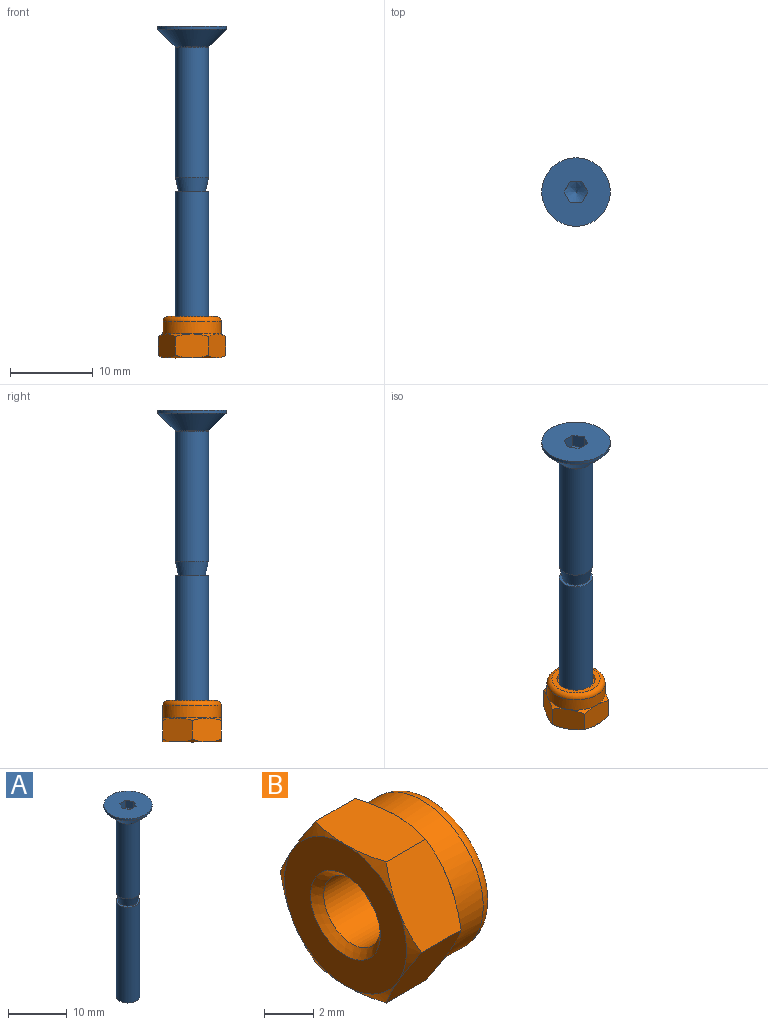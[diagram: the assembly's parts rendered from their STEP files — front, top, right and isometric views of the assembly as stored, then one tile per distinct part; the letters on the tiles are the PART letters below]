
ASSEMBLY  parts=2 mates=1
PART A: 16 faces, bbox 8.4x8.4x40.1 mm
  f0: plane 4x4mm, normal (0,0,-1), area 12.6mm2, adj f1
  f1: revolved ~20x4mm, area 251.3mm2, adj f0,f2
  f2: plane 4x4mm, normal (0,0,1), area 4.3mm2, adj f1,f3
  f3: revolved ~4x4mm, area 20.4mm2, adj f2,f4
  f4: revolved ~15.66x4mm, area 196.7mm2, adj f3,f5
  f5: revolved ~4.09x4.09mm, area 1.6mm2, adj f4,f6
  f6: revolved ~8.25x8.25mm, area 56.9mm2, adj f5,f7
  f7: revolved ~8.25x8.25mm, area 21mm2, adj f6,f8
  f8: plane 8.25x8.25mm, normal (0,0,1), area 48mm2, adj f7,f9,f10,f11,f12,f13,f14
  f9: plane 1.61x1.25mm, normal (-0.87,0.5,0), area 2.3mm2, adj f8,f10,f14,f15
  f10: plane 1.73x1.56mm, normal (0,1,0), area 2.3mm2, adj f8,f9,f11,f15
  f11: plane 1.61x1.25mm, normal (0.87,0.5,0), area 2.3mm2, adj f8,f10,f12,f15
  f12: plane 1.61x1.25mm, normal (0.87,-0.5,0), area 2.3mm2, adj f8,f11,f13,f15
  f13: plane 1.73x1.56mm, normal (0,-1,0), area 2.3mm2, adj f8,f12,f14,f15
  f14: plane 1.61x1.25mm, normal (-0.87,-0.5,0), area 2.3mm2, adj f8,f9,f13,f15
  f15: revolved ~2.89x2.89mm, area 6.4mm2, adj f9,f10,f11,f12,f13,f14
PART B: 30 faces, bbox 5x8.1x8.1 mm
  f0: cone r=1.81mm half-angle=45deg, axis (-1,0,0), area 6.1mm2, adj f1,f29
  f1: cylinder r=1.62mm len=3.24mm, axis (1,0,0), area 21.8mm2, adj f0,f2
  f2: cone r=1.81mm half-angle=45deg, axis (1,0,0), area 6.1mm2, adj f1,f3
  f3: cylinder r=2mm len=4mm, axis (1,0,0), area 6.6mm2, adj f2,f28
  f4: cylinder r=1.62mm len=3.24mm, axis (1,0,0), area 10.7mm2, adj f27,f28
  f5: cylinder r=2.3mm len=4.6mm, axis (1,0,0), area 7.6mm2, adj f26,f27
  f6: torus R=2.9mm, axis (1,0,0), area 19.4mm2, adj f9,f26
  f7: cone r=4.38mm half-angle=60deg, axis (-1,0,0), area 0.8mm2, adj f9,f13,f15
  f8: cone r=4.38mm half-angle=60deg, axis (-1,0,0), area 0.8mm2, adj f9,f12,f17
  f9: cylinder r=3.5mm len=7mm, axis (1,0,0), area 33mm2, adj f6,f7,f8,f22,f23,f24,f25
  f10: cone r=4.38mm half-angle=60deg, axis (1,0,0), area 0.8mm2, adj f13,f15,f29
  f11: cone r=4.38mm half-angle=60deg, axis (1,0,0), area 0.8mm2, adj f12,f17,f29
  f12: plane 3.5x2.9mm, normal (0,-0.87,0.5), area 10.9mm2, adj f8,f11,f14,f17,f20,f22
  f13: plane 3.5x2.9mm, normal (0,0.87,0.5), area 10.9mm2, adj f7,f10,f14,f15,f21,f25
  f14: plane 4.04x2.9mm, normal (0,0,1), area 10.9mm2, adj f12,f13,f20,f21,f22,f25
  f15: plane 3.5x2.9mm, normal (0,0.87,-0.5), area 10.9mm2, adj f7,f10,f13,f16,f18,f24
  f16: plane 4.04x2.9mm, normal (0,0,-1), area 10.9mm2, adj f15,f17,f18,f19,f23,f24
  f17: plane 3.5x2.9mm, normal (0,-0.87,-0.5), area 10.9mm2, adj f8,f11,f12,f16,f19,f23
  f18: cone r=4.38mm half-angle=60deg, axis (1,0,0), area 0.8mm2, adj f15,f16,f29
  f19: cone r=4.38mm half-angle=60deg, axis (1,0,0), area 0.8mm2, adj f16,f17,f29
  f20: cone r=4.38mm half-angle=60deg, axis (1,0,0), area 0.8mm2, adj f12,f14,f29
  f21: cone r=4.38mm half-angle=60deg, axis (1,0,0), area 0.8mm2, adj f13,f14,f29
  f22: cone r=4.38mm half-angle=60deg, axis (-1,0,0), area 0.8mm2, adj f9,f12,f14
  f23: cone r=4.38mm half-angle=60deg, axis (-1,0,0), area 0.8mm2, adj f9,f16,f17
  f24: cone r=4.38mm half-angle=60deg, axis (-1,0,0), area 0.8mm2, adj f9,f15,f16
  f25: cone r=4.38mm half-angle=60deg, axis (-1,0,0), area 0.8mm2, adj f9,f13,f14
  f26: plane 5.8x5.8mm, normal (1,0,0), area 9.8mm2, adj f5,f6
  f27: plane 4.6x4.6mm, normal (1,0,0), area 8.4mm2, adj f4,f5
  f28: plane 4x4mm, normal (-1,0,0), area 4.3mm2, adj f3,f4
  f29: plane 7x7mm, normal (-1,0,0), area 25.9mm2, adj f0,f10,f11,f18,f19,f20,f21
PLACE A t=(7.37,10.96,-20.1)mm
PLACE B rot(axis=(0.58,-0.58,0.58),120deg) t=(7.37,10.96,-60.1)mm
MATE revolute B.f7 <-> A.f0  axis (0,0,-1) through (7.37,10.96,-60.1)mm
